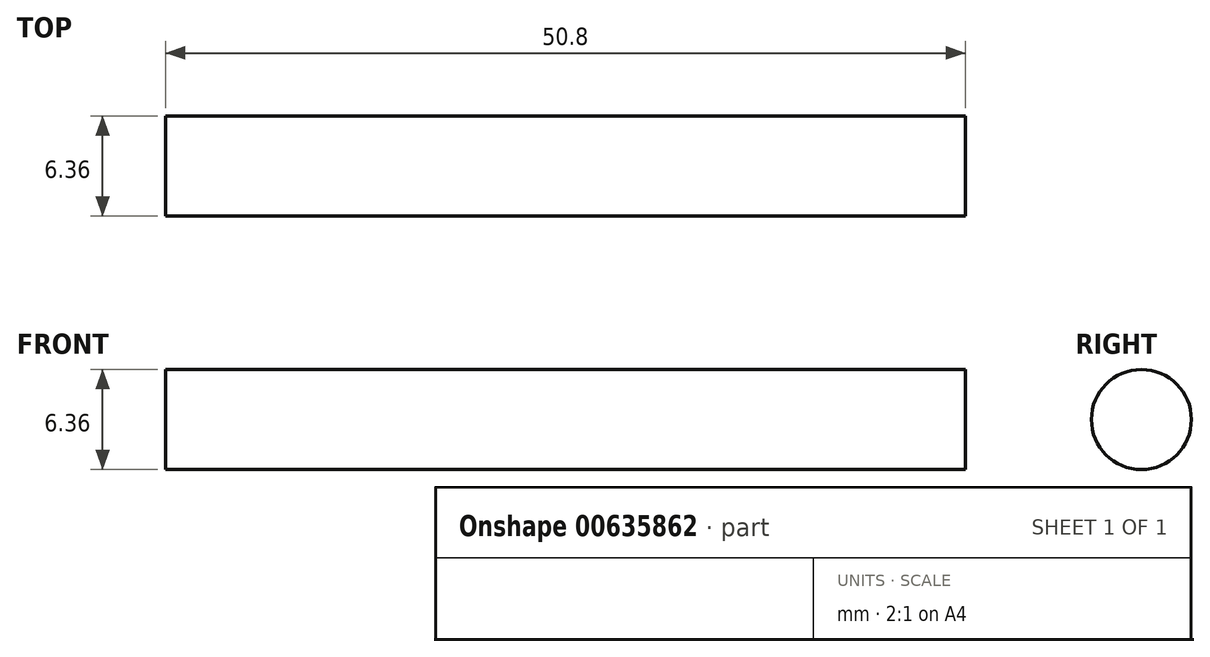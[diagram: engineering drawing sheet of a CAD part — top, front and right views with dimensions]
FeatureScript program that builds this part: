
annotation { "Feature Type Name" : "Feature", "Feature Type Description" : "" }
export const myFeature = defineFeature(function(context is Context, id is Id, definition is map)
    precondition{}
    {
        {
            var Q0;
            Q0=qCreatedBy(makeId("Right.planeOp"),FACE);
            var sketch = newSketch(context, id + "F0", { "sketchPlane" : qUnion([Q0])});
            skCircle(sketch, "E0", {"center": v(0, 0) * mm, "radius": 3.18 * mm});
            skSolve(sketch);
        }
        {
            var Q0;
            Q0=makeQuery(id+"F0.imprint","IMPRINT",FACE,{"disambiguationData":[TD([[makeQuery(id+"F0.imprint","IMPRINT",EDGE,{"derivedFrom":sQuery(id+"F0.wireOp",EDGE,"E0")}),1.0]])]});
            extrude(context, id + "F1", {"entities" : qUnion([Q0]), "depth" : 50.8 * mm, "offsetDistance" : 25.4 * mm});
        }
    });
